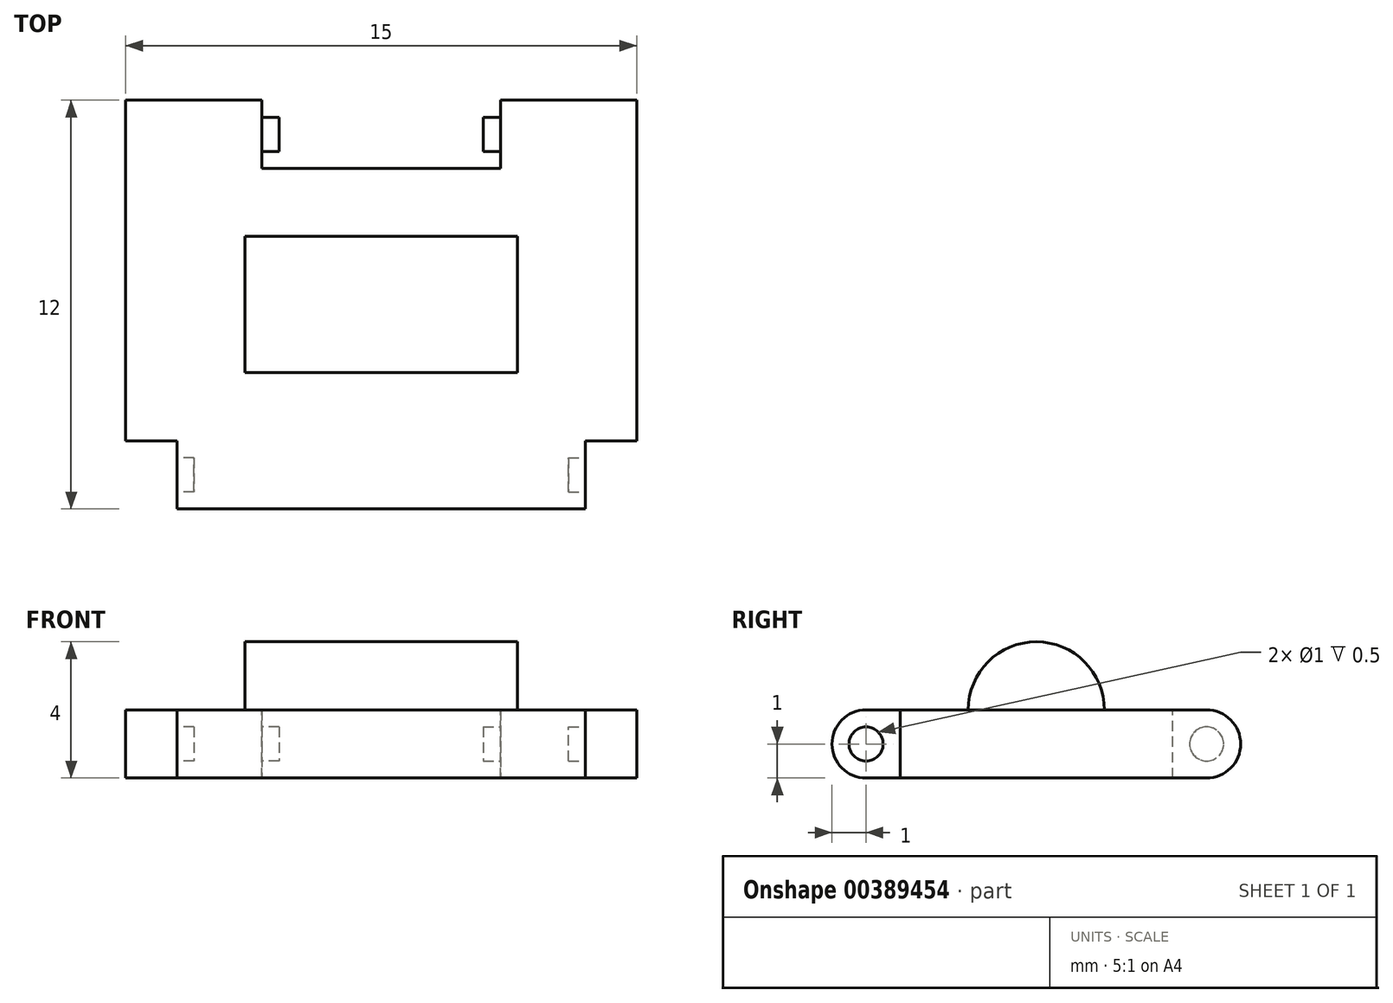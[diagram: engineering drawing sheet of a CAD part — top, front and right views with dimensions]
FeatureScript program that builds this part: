
annotation { "Feature Type Name" : "Feature", "Feature Type Description" : "" }
export const myFeature = defineFeature(function(context is Context, id is Id, definition is map)
    precondition{}
    {
        {
            var Q0;
            Q0=qCreatedBy(makeId("Right.planeOp"),FACE);
            var sketch = newSketch(context, id + "F0", { "sketchPlane" : qUnion([Q0])});
            skLineSegment(sketch, "E0.bottom", {"start": v(5, 1) * mm, "end": v(-5, 1) * mm});
            skLineSegment(sketch, "E0.top", {"start": v(5, -1) * mm, "end": v(-5, -1) * mm});
            skPoint(sketch, "E0.middle", {"position": v(0, 0) * mm});
            skArc(sketch, "E1", {"start": v(5, -1) * mm, "mid": v(6, 0) * mm, "end": v(5, 1) * mm});
            skArc(sketch, "E2", {"start": v(-5, 1) * mm, "mid": v(-6, 0) * mm, "end": v(-5, -1) * mm});
            skSolve(sketch);
        }
        {
            var Q0;
            Q0=qSketchRegion(id+"F0",true);
            extrude(context, id + "F1", {"entities" : qUnion([Q0]), "endBound" : BoundingType.SYMMETRIC, "depth" : 15 * mm});
        }
        {
            var Q0;
            Q0=makeQuery(id+"F1.opExtrude","SWEPT_FACE",FACE,{"disambiguationData":[OSD([sQuery(id+"F0.wireOp",EDGE,"E0.bottom")])]});
            var sketch = newSketch(context, id + "F2", { "sketchPlane" : qUnion([Q0])});
            skLineSegment(sketch, "E3.bottom", {"start": v(3.5, 6.1) * mm, "end": v(-3.5, 6.1) * mm});
            skLineSegment(sketch, "E3.left", {"start": v(3.5, 6.1) * mm, "end": v(3.5, 4) * mm});
            skLineSegment(sketch, "E3.right", {"start": v(-3.5, 6.1) * mm, "end": v(-3.5, 4) * mm});
            skPoint(sketch, "E3.middle", {"position": v(0, 5) * mm});
            skLineSegment(sketch, "E4", {"start": v(-3.5, 4) * mm, "end": v(3.5, 4) * mm});
            skLineSegment(sketch, "E5.bottom", {"start": v(-7.5, -4) * mm, "end": v(-6, -4) * mm});
            skLineSegment(sketch, "E5.top", {"start": v(-7.5, -6.5) * mm, "end": v(-6, -6.5) * mm});
            skLineSegment(sketch, "E5.left", {"start": v(-7.5, -4) * mm, "end": v(-7.5, -6.5) * mm});
            skLineSegment(sketch, "E5.right", {"start": v(-6, -4) * mm, "end": v(-6, -6.5) * mm});
            skLineSegment(sketch, "E6.bottom", {"start": v(7.5, -4) * mm, "end": v(6, -4) * mm});
            skLineSegment(sketch, "E6.top", {"start": v(7.5, -7.1) * mm, "end": v(6, -7.1) * mm});
            skLineSegment(sketch, "E6.left", {"start": v(7.5, -4) * mm, "end": v(7.5, -7.1) * mm});
            skLineSegment(sketch, "E6.right", {"start": v(6, -4) * mm, "end": v(6, -7.1) * mm});
            skSolve(sketch);
        }
        {
            var Q0;
            Q0=qSketchRegion(id+"F2",true);
            extrude(context, id + "F3", {"entities" : qUnion([Q0]), "operationType" : NewBodyOperationType.REMOVE, "oppositeDirection" : true, "depth" : 5 * mm});
        }
        {
            var Q0;
            Q0=makeQuery(id+"F3.boolean.opBoolean","COPY",FACE,{"derivedFrom":makeQuery(id+"F3.opExtrude","SWEPT_FACE",FACE,{"disambiguationData":[OSD([sQuery(id+"F2.wireOp",EDGE,"E5.right")])]})});
            var sketch = newSketch(context, id + "F4", { "sketchPlane" : qUnion([Q0])});
            skCircle(sketch, "E7", {"center": v(5, 0) * mm, "radius": 0.5 * mm});
            skSolve(sketch);
        }
        {
            var Q0;
            Q0=qSketchRegion(id+"F4",true);
            extrude(context, id + "F5", {"entities" : qUnion([Q0]), "operationType" : NewBodyOperationType.REMOVE, "oppositeDirection" : true, "depth" : 0.5 * mm});
        }
        {
            var Q0;
            Q0=makeQuery(id+"F3.boolean.opBoolean","COPY",FACE,{"derivedFrom":makeQuery(id+"F3.opExtrude","SWEPT_FACE",FACE,{"disambiguationData":[OSD([sQuery(id+"F2.wireOp",EDGE,"E6.right")])]})});
            var sketch = newSketch(context, id + "F6", { "sketchPlane" : qUnion([Q0])});
            skCircle(sketch, "E8", {"center": v(-5, 0) * mm, "radius": 0.5 * mm});
            skSolve(sketch);
        }
        {
            var Q0;
            Q0=qSketchRegion(id+"F6",true);
            extrude(context, id + "F7", {"entities" : qUnion([Q0]), "operationType" : NewBodyOperationType.REMOVE, "oppositeDirection" : true, "depth" : 0.5 * mm});
        }
        {
            var Q0;
            Q0=makeQuery(id+"F3.boolean.opBoolean","COPY",FACE,{"derivedFrom":makeQuery(id+"F3.opExtrude","SWEPT_FACE",FACE,{"disambiguationData":[OSD([sQuery(id+"F2.wireOp",EDGE,"E3.right")])]})});
            var sketch = newSketch(context, id + "F8", { "sketchPlane" : qUnion([Q0])});
            skCircle(sketch, "E9", {"center": v(5, 0) * mm, "radius": 0.5 * mm});
            skSolve(sketch);
        }
        {
            var Q0;
            Q0=qSketchRegion(id+"F8",true);
            extrude(context, id + "F9", {"entities" : qUnion([Q0]), "operationType" : NewBodyOperationType.ADD, "depth" : 0.5 * mm});
        }
        {
            var Q0;
            Q0=makeQuery(id+"F3.boolean.opBoolean","COPY",FACE,{"derivedFrom":makeQuery(id+"F3.opExtrude","SWEPT_FACE",FACE,{"disambiguationData":[OSD([sQuery(id+"F2.wireOp",EDGE,"E3.left")])]})});
            var sketch = newSketch(context, id + "F10", { "sketchPlane" : qUnion([Q0])});
            skCircle(sketch, "E10", {"center": v(-5, 0) * mm, "radius": 0.5 * mm});
            skSolve(sketch);
        }
        {
            var Q0;
            Q0=qSketchRegion(id+"F10",true);
            extrude(context, id + "F11", {"entities" : qUnion([Q0]), "operationType" : NewBodyOperationType.ADD, "depth" : 0.5 * mm});
        }
        {
            var Q0;
            Q0=qCreatedBy(makeId("Right.planeOp"),FACE);
            var sketch = newSketch(context, id + "F12", { "sketchPlane" : qUnion([Q0])});
            skPoint(sketch, "E11", {"position": v(-2, 1) * mm});
            skPoint(sketch, "E12", {"position": v(2, 1) * mm});
            skArc(sketch, "E13", {"start": v(2, 1) * mm, "mid": v(0, 3) * mm, "end": v(-2, 1) * mm});
            skLineSegment(sketch, "E14", {"start": v(-2, 1) * mm, "end": v(2, 1) * mm});
            skSolve(sketch);
        }
        {
            var Q0;
            Q0=qSketchRegion(id+"F12",true);
            extrude(context, id + "F13", {"entities" : qUnion([Q0]), "operationType" : NewBodyOperationType.ADD, "endBound" : BoundingType.SYMMETRIC, "depth" : 8 * mm});
        }
    });
